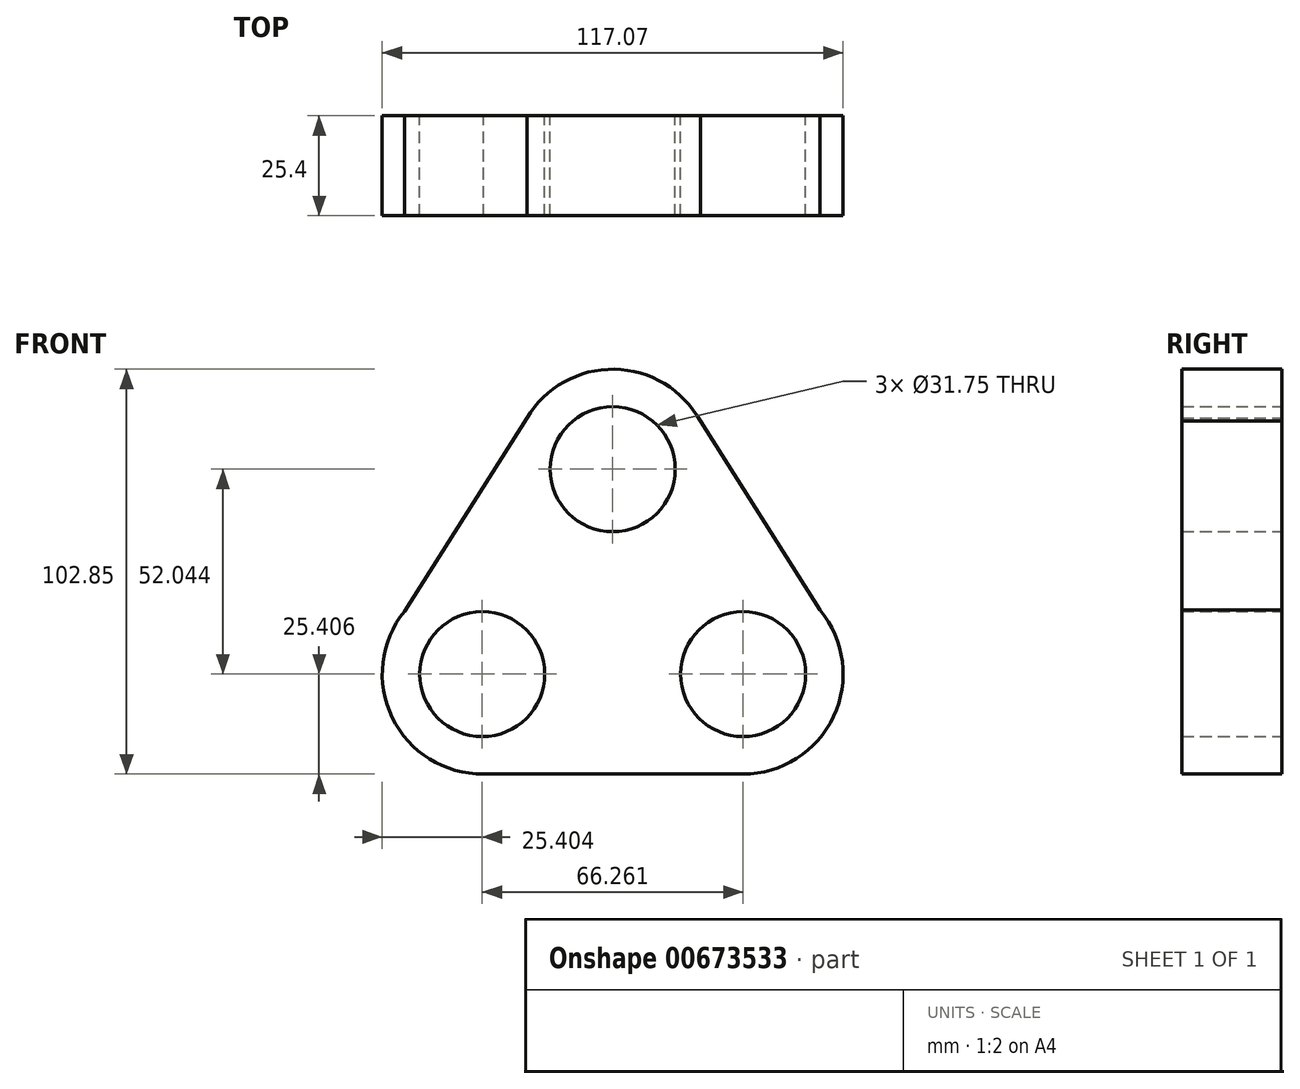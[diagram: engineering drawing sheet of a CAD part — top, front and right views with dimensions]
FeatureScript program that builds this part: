
annotation { "Feature Type Name" : "Feature", "Feature Type Description" : "" }
export const myFeature = defineFeature(function(context is Context, id is Id, definition is map)
    precondition{}
    {
        {
            var Q0;
            Q0=qCreatedBy(makeId("Front.planeOp"),FACE);
            var sketch = newSketch(context, id + "F0", { "sketchPlane" : qUnion([Q0])});
            skLineSegment(sketch, "E0.top", {"start": v(-23.6, -37.7) * mm, "end": v(42.66, -37.7) * mm});
            skLineSegment(sketch, "E0.left", {"start": v(-49, -12.04) * mm, "end": v(-49, -12.3) * mm});
            skPoint(sketch, "E1.visualSharp", {"position": v(-49, -37.7) * mm});
            skArc(sketch, "E1.filletArc", {"start": v(-49, -12.3) * mm, "mid": v(-41.57, -30.26) * mm, "end": v(-23.6, -37.7) * mm});
            skPoint(sketch, "E2.visualSharp", {"position": v(68.06, -37.7) * mm});
            skArc(sketch, "E2.filletArc", {"start": v(42.66, -37.7) * mm, "mid": v(60.62, -30.26) * mm, "end": v(68.06, -12.3) * mm});
            skArc(sketch, "E3", {"start": v(-43.36, 3.66) * mm, "mid": v(-46.47, -23.37) * mm, "end": v(-23.34, -37.7) * mm});
            skArc(sketch, "E4", {"start": v(31.8, 51.96) * mm, "mid": v(9.98, 65.14) * mm, "end": v(-12.3, 52.74) * mm});
            skArc(sketch, "E5", {"start": v(42.66, -37.7) * mm, "mid": v(65.66, -23.08) * mm, "end": v(62.17, 3.95) * mm});
            skLineSegment(sketch, "E6", {"start": v(-11.56, 53.9) * mm, "end": v(-43.36, 3.66) * mm});
            skLineSegment(sketch, "E7", {"start": v(30.1, 54.63) * mm, "end": v(62.17, 3.95) * mm});
            skCircle(sketch, "E8", {"center": v(-23.6, -12.3) * mm, "radius": 15.88 * mm});
            skCircle(sketch, "E9", {"center": v(42.66, -12.3) * mm, "radius": 15.88 * mm});
            skCircle(sketch, "E10", {"center": v(9.52, 39.74) * mm, "radius": 15.88 * mm});
            skPoint(sketch, "E11.orphan", {"position": v(-49, 39.74) * mm});
            skPoint(sketch, "E0.right.start.orphan", {"position": v(68.06, 39.74) * mm});
            skLineSegment(sketch, "E12.trimOffspring", {"start": v(26.78, -12.3) * mm, "end": v(42.66, -12.3) * mm});
            skSolve(sketch);
        }
        {
            var Q0;
            Q0 = qSketchRegion(id + "F0", true);
            extrude(context, id + "F1", {"entities" : qUnion([Q0]), "depth" : 25.4 * mm, "offsetDistance" : 25.4 * mm});
        }
    });
